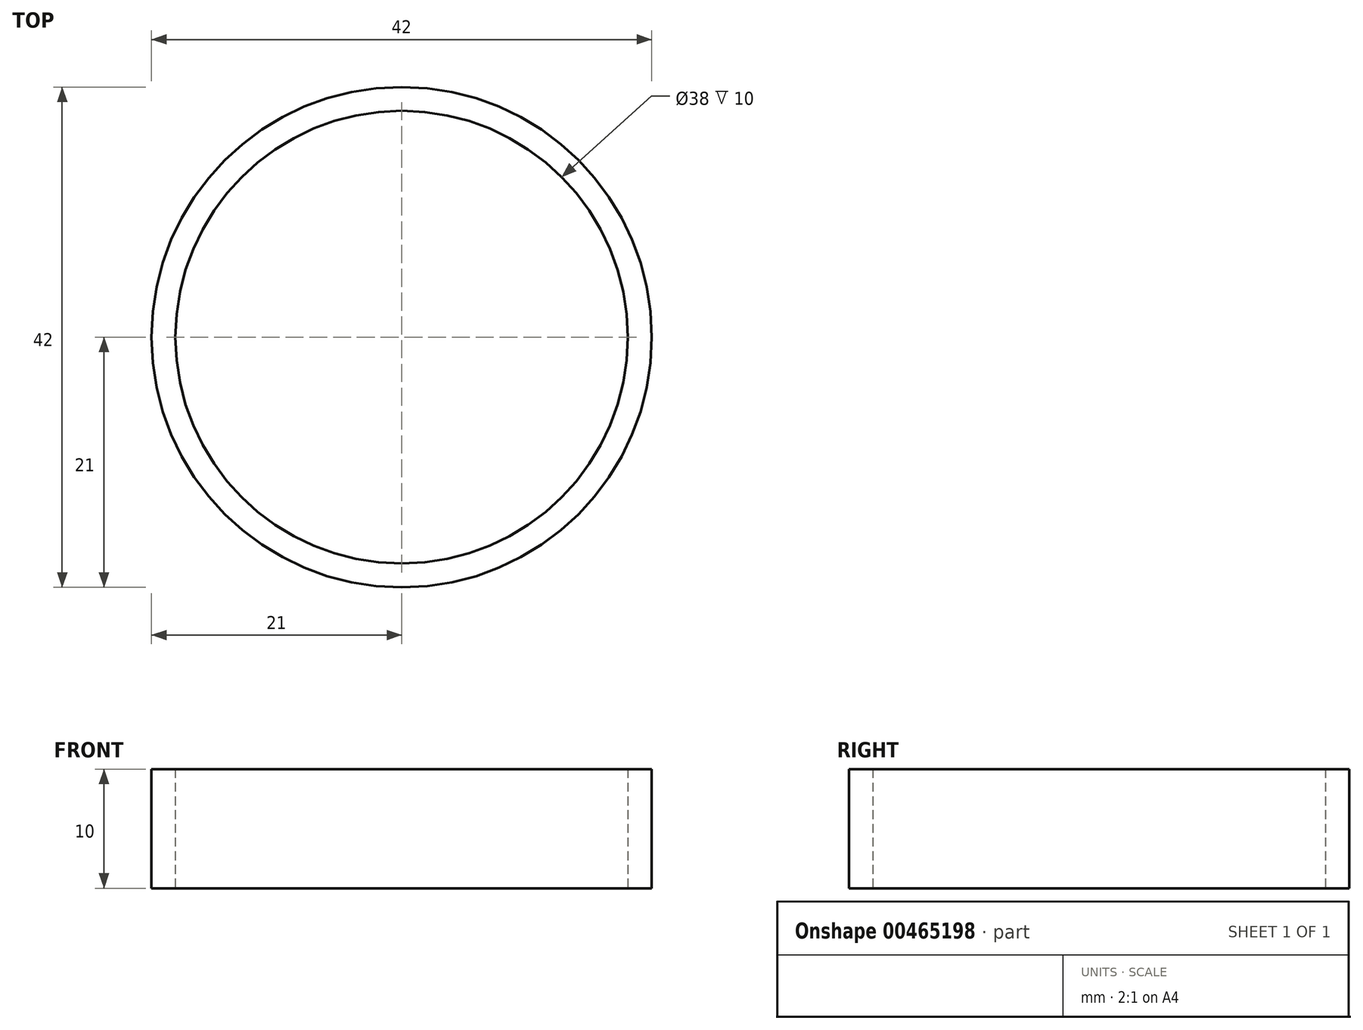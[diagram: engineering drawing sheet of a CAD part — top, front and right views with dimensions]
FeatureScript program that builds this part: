
annotation { "Feature Type Name" : "Feature", "Feature Type Description" : "" }
export const myFeature = defineFeature(function(context is Context, id is Id, definition is map)
    precondition{}
    {
        {
            var Q0;
            Q0=qCreatedBy(makeId("Top.planeOp"),FACE);
            var sketch = newSketch(context, id + "F0", { "sketchPlane" : qUnion([Q0])});
            skCircle(sketch, "E0", {"center": v(0, 0) * mm, "radius": 19 * mm});
            skCircle(sketch, "E1", {"center": v(0, 0) * mm, "radius": 21 * mm});
            skSolve(sketch);
        }
        {
            var Q0;
            Q0=makeQuery(id+"F0.imprint","IMPRINT",FACE,{"disambiguationData":[TD([[makeQuery(id+"F0.imprint","IMPRINT",EDGE,{"derivedFrom":sQuery(id+"F0.wireOp",EDGE,"E0")}),-1.0]])]});
            extrude(context, id + "F1", {"entities" : qUnion([Q0]), "depth" : 10 * mm});
        }
    });
